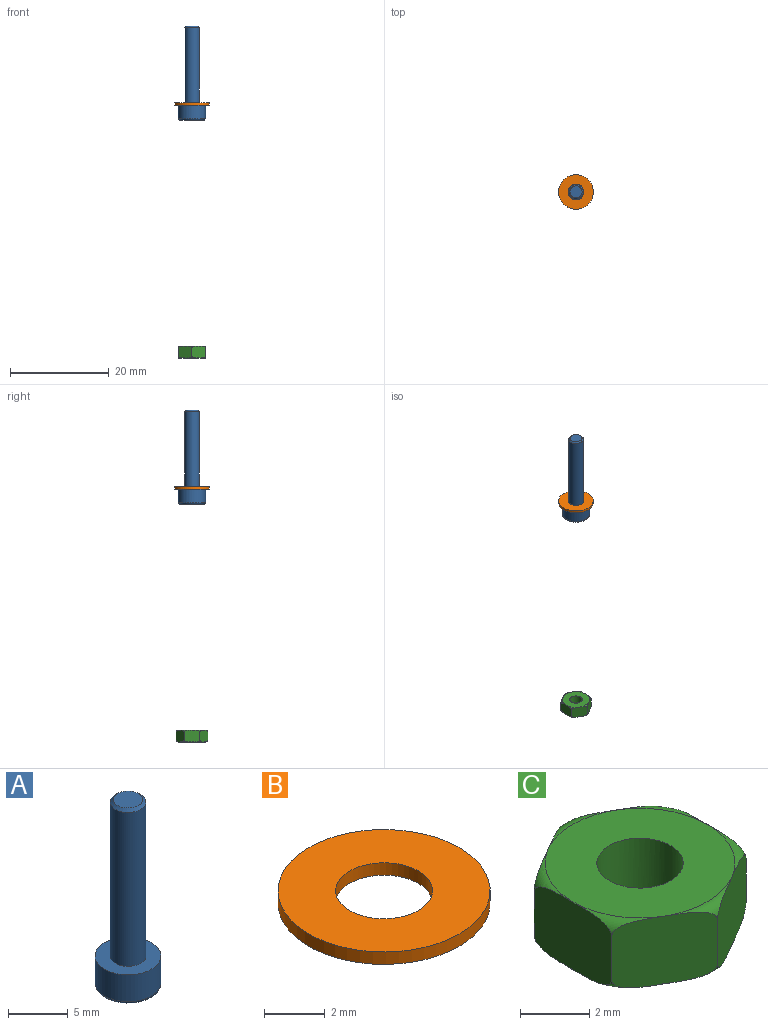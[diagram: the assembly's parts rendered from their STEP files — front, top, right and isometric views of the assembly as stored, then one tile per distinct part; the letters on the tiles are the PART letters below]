
ASSEMBLY  parts=3 mates=3
PART A: 14 faces, bbox 6x6x19 mm
  f0: plane 4.95x4.95mm, normal (0,0,-1), area 13.5mm2, adj f3,f4,f5,f6,f7,f8,f9
  f1: cylinder r=2.75mm len=5.5mm, axis (0,0,1), area 47.1mm2, adj f2,f3
  f2: plane 5.5x5.5mm, normal (0,0,1), area 16.7mm2, adj f1,f11
  f3: torus R=2.48mm, axis (0,0,-1), area 7.2mm2, adj f0,f1
  f4: plane 1.5x1.49mm, normal (-1,0,0), area 2.2mm2, adj f0,f5,f9,f10
  f5: plane 1.5x1.29mm, normal (-0.5,-0.87,0), area 2.2mm2, adj f0,f4,f6,f10
  f6: plane 1.5x1.29mm, normal (0.5,-0.87,0), area 2.2mm2, adj f0,f5,f7,f10
  f7: plane 1.5x1.49mm, normal (1,0,0), area 2.2mm2, adj f0,f6,f8,f10
  f8: plane 1.5x1.29mm, normal (0.5,0.87,0), area 2.2mm2, adj f0,f7,f9,f10
  f9: plane 1.5x1.29mm, normal (-0.5,0.87,0), area 2.2mm2, adj f0,f4,f8,f10
  f10: plane 2.98x2.58mm, normal (0,0,-1), area 5.8mm2, adj f4,f5,f6,f7,f8,f9
  f11: cylinder r=1.5mm len=15.73mm, axis (0,0,-1), area 148.2mm2, adj f2,f13
  f12: plane 2.46x2.46mm, normal (0,0,1), area 4.7mm2, adj f13
  f13: cone r=1.23mm half-angle=45deg, axis (0,0,-1), area 3.3mm2, adj f11,f12
PART B: 4 faces, bbox 7x7x0.5 mm
  f0: cylinder r=1.6mm len=3.2mm, axis (0,0,-1), area 5mm2, adj f2,f3
  f1: cylinder r=3.5mm len=7mm, axis (0,0,-1), area 11mm2, adj f2,f3
  f2: plane 7x7mm, normal (0,0,1), area 30.4mm2, adj f0,f1
  f3: plane 7x7mm, normal (0,0,-1), area 30.4mm2, adj f0,f1
PART C: 11 faces, bbox 6.9x6.9x2.4 mm
  f0: plane 5.49x5.49mm, normal (0,0,1), area 18.8mm2, adj f1,f10
  f1: torus R=2.75mm, axis (0,0,-1), area 2.8mm2, adj f0,f2,f3,f4,f5,f6,f7
  f2: plane 2.75x2.4mm, normal (0.5,0.87,0), area 7.3mm2, adj f1,f3,f7,f9
  f3: plane 3.18x2.4mm, normal (1,0,0), area 7.3mm2, adj f1,f2,f4,f9
  f4: plane 2.75x2.4mm, normal (0.5,-0.87,0), area 7.3mm2, adj f1,f3,f5,f9
  f5: plane 2.75x2.4mm, normal (-0.5,-0.87,0), area 7.3mm2, adj f1,f4,f6,f9
  f6: plane 3.18x2.4mm, normal (-1,0,0), area 7.3mm2, adj f1,f5,f7,f9
  f7: plane 2.75x2.4mm, normal (-0.5,0.87,0), area 7.3mm2, adj f1,f2,f6,f9
  f8: plane 5.49x5.49mm, normal (0,0,-1), area 18.8mm2, adj f9,f10
  f9: torus R=2.75mm, axis (0,0,-1), area 2.8mm2, adj f2,f3,f4,f5,f6,f7,f8
  f10: cylinder r=1.25mm len=2.5mm, axis (0,0,-1), area 18.8mm2, adj f0,f8
PLACE A t=(-18.55,-3.45,7.62)mm
PLACE B rot(axis=(1,0,0),180deg) t=(41.45,-13.45,8.12)mm
PLACE C t=(11.45,16.55,-43.47)mm
MATE cylindrical B.f0 <-> A.f1  axis (0,0,1) through (31.45,-3.45,7.87)mm
MATE planar B.f0 <-> A.f1  axis (0,0,-1) through (31.45,-3.45,7.62)mm
MATE cylindrical A.f1 <-> C.f1  axis (0,0,-1) through (31.45,-3.45,15.48)mm
